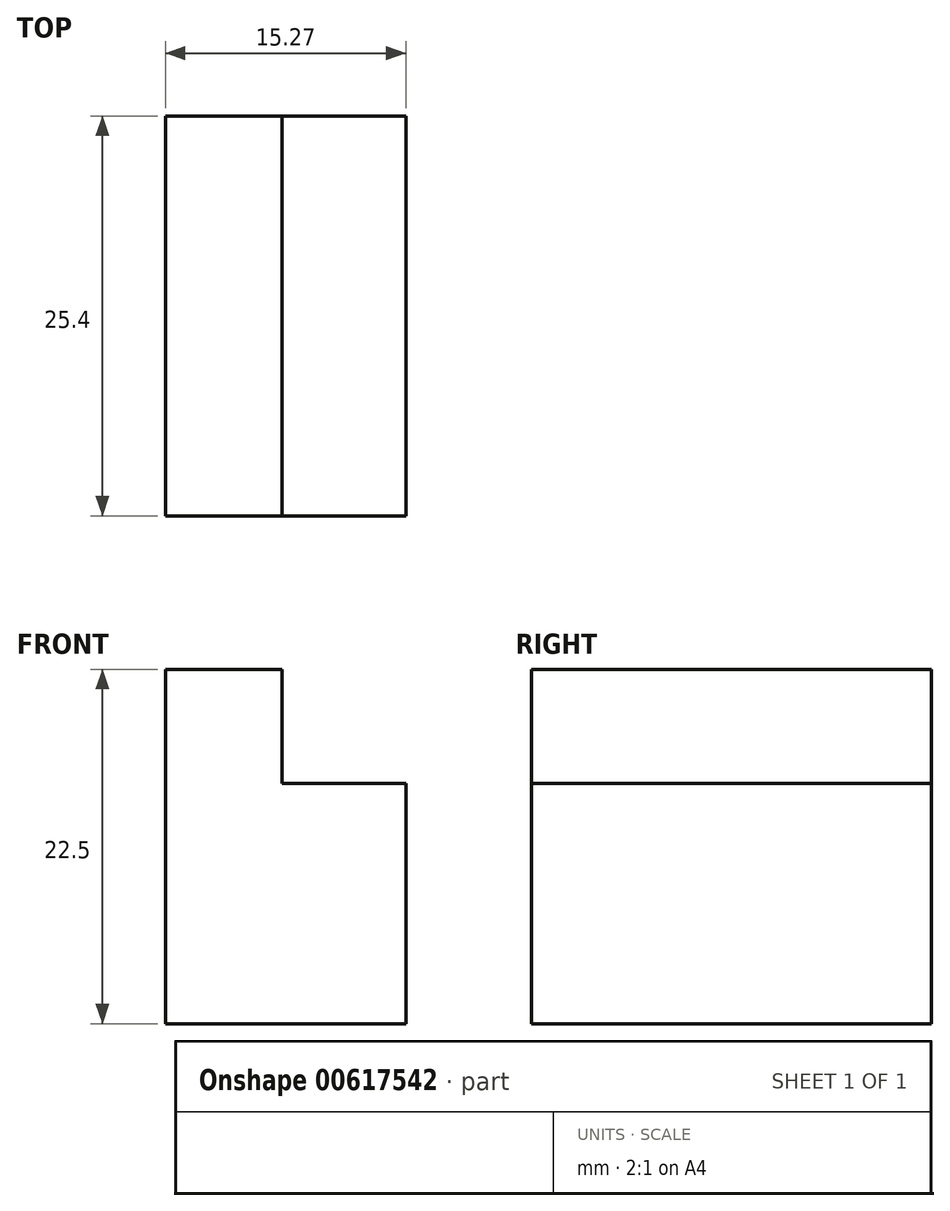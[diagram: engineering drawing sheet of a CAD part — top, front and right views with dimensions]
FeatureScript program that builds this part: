
annotation { "Feature Type Name" : "Feature", "Feature Type Description" : "" }
export const myFeature = defineFeature(function(context is Context, id is Id, definition is map)
    precondition{}
    {
        {
            var Q0;
            Q0=qCreatedBy(makeId("Front.planeOp"),FACE);
            var sketch = newSketch(context, id + "F0", { "sketchPlane" : qUnion([Q0])});
            skLineSegment(sketch, "E0", {"start": v(0, 0) * mm, "end": v(15.27, 0) * mm});
            skLineSegment(sketch, "E1", {"start": v(15.27, 0) * mm, "end": v(15.27, 15.27) * mm});
            skLineSegment(sketch, "E2", {"start": v(15.27, 15.27) * mm, "end": v(7.4, 15.27) * mm});
            skLineSegment(sketch, "E3", {"start": v(7.4, 15.27) * mm, "end": v(7.4, 22.5) * mm});
            skLineSegment(sketch, "E4", {"start": v(7.4, 22.5) * mm, "end": v(0, 22.5) * mm});
            skLineSegment(sketch, "E5", {"start": v(0, 22.5) * mm, "end": v(0, 0) * mm});
            skSolve(sketch);
        }
        {
            var Q0;
            Q0 = qSketchRegion(id + "F0", true);
            extrude(context, id + "F1", {"entities" : qUnion([Q0]), "depth" : 25.4 * mm, "offsetDistance" : 25.4 * mm});
        }
    });
